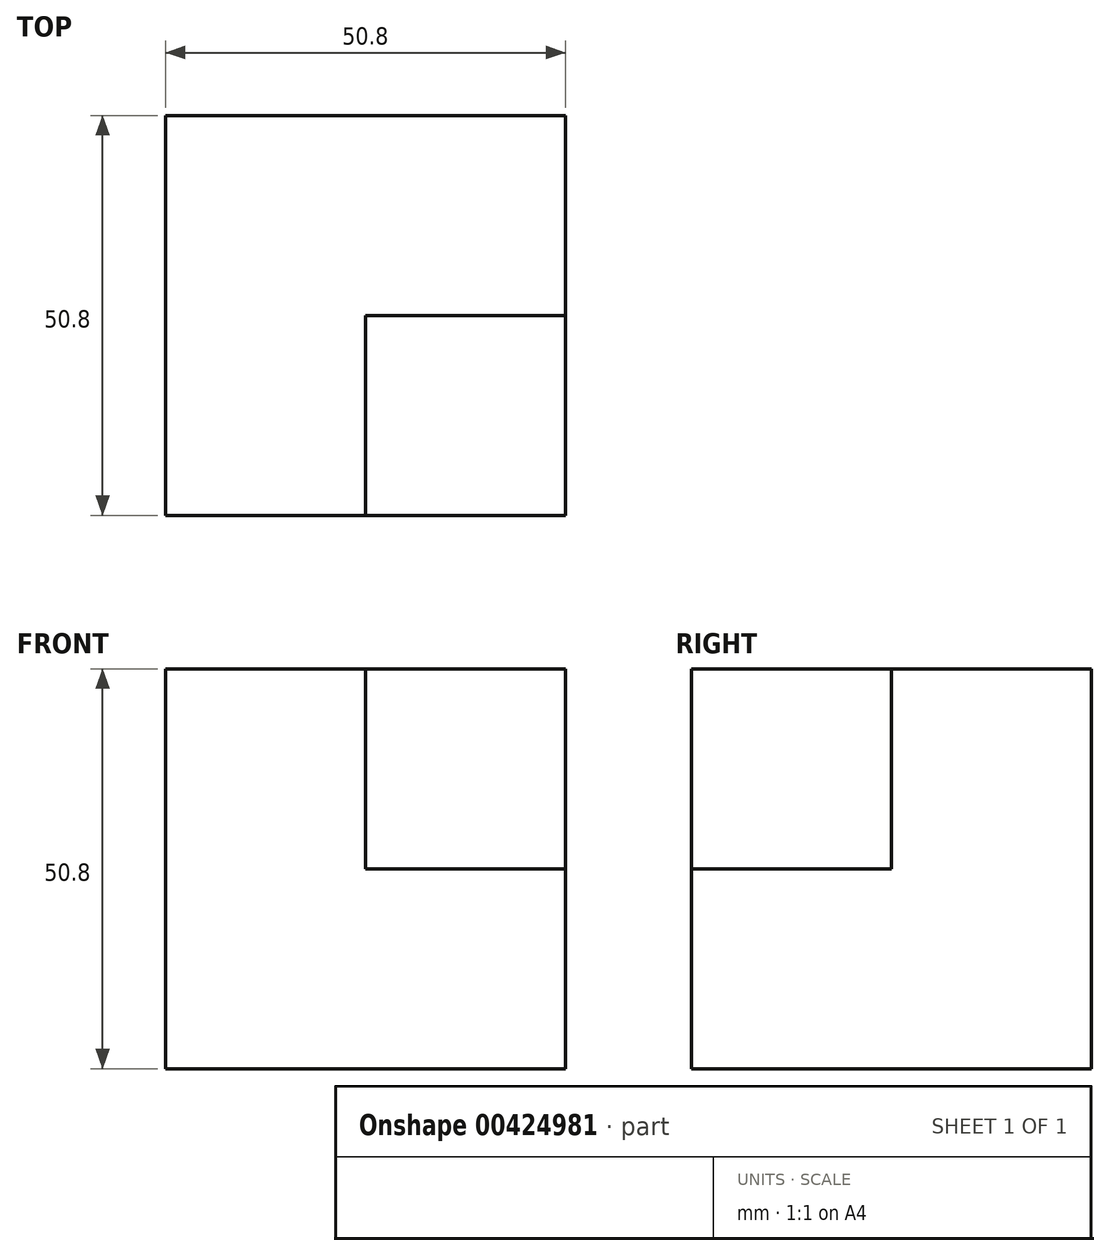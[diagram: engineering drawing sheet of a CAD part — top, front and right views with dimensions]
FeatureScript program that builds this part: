
annotation { "Feature Type Name" : "Feature", "Feature Type Description" : "" }
export const myFeature = defineFeature(function(context is Context, id is Id, definition is map)
    precondition{}
    {
        {
            var Q0;
            Q0=qCreatedBy(makeId("Front.planeOp"),FACE);
            var sketch = newSketch(context, id + "F0", { "sketchPlane" : qUnion([Q0])});
            skLineSegment(sketch, "E0", {"start": v(0, 0) * mm, "end": v(-50.8, 0) * mm});
            skLineSegment(sketch, "E1", {"start": v(-50.8, 0) * mm, "end": v(-50.8, 50.8) * mm});
            skLineSegment(sketch, "E2", {"start": v(-50.8, 50.8) * mm, "end": v(0, 50.8) * mm});
            skLineSegment(sketch, "E3", {"start": v(0, 50.8) * mm, "end": v(0, 0) * mm});
            skSolve(sketch);
        }
        {
            var Q0;
            Q0 = qSketchRegion(id + "F0", true);
            var Q1;
            Q1=makeQuery(id+"F0.imprint","IMPRINT",FACE,{"disambiguationData":[TD([[makeQuery(id+"F0.imprint","IMPRINT",EDGE,{"derivedFrom":sQuery(id+"F0.wireOp",EDGE,"E0")}),-1.0]])]});
            extrude(context, id + "F1", {"entities" : qUnion([Q0, Q1]), "depth" : 50.8 * mm});
        }
        {
            var Q0;
            Q0=makeQuery(id+"F1.opExtrude","CAP_FACE",FACE,{"disambiguationData":[OSD([sQuery(id+"F0.wireOp",EDGE,"E0"),sQuery(id+"F0.wireOp",EDGE,"E1"),sQuery(id+"F0.wireOp",EDGE,"E2"),sQuery(id+"F0.wireOp",EDGE,"E3")])],"isStart":false});
            var sketch = newSketch(context, id + "F2", { "sketchPlane" : qUnion([Q0])});
            skLineSegment(sketch, "E4", {"start": v(0, 50.8) * mm, "end": v(-25.4, 50.8) * mm});
            skLineSegment(sketch, "E5", {"start": v(-25.4, 50.8) * mm, "end": v(-25.4, 25.4) * mm});
            skLineSegment(sketch, "E6", {"start": v(-25.4, 25.4) * mm, "end": v(0, 25.4) * mm});
            skLineSegment(sketch, "E7", {"start": v(0, 25.4) * mm, "end": v(0, 50.8) * mm});
            skSolve(sketch);
        }
        {
            var Q0;
            Q0 = qSketchRegion(id + "F2", true);
            extrude(context, id + "F3", {"entities" : qUnion([Q0]), "operationType" : NewBodyOperationType.REMOVE, "oppositeDirection" : true, "depth" : 25.4 * mm});
        }
    });
